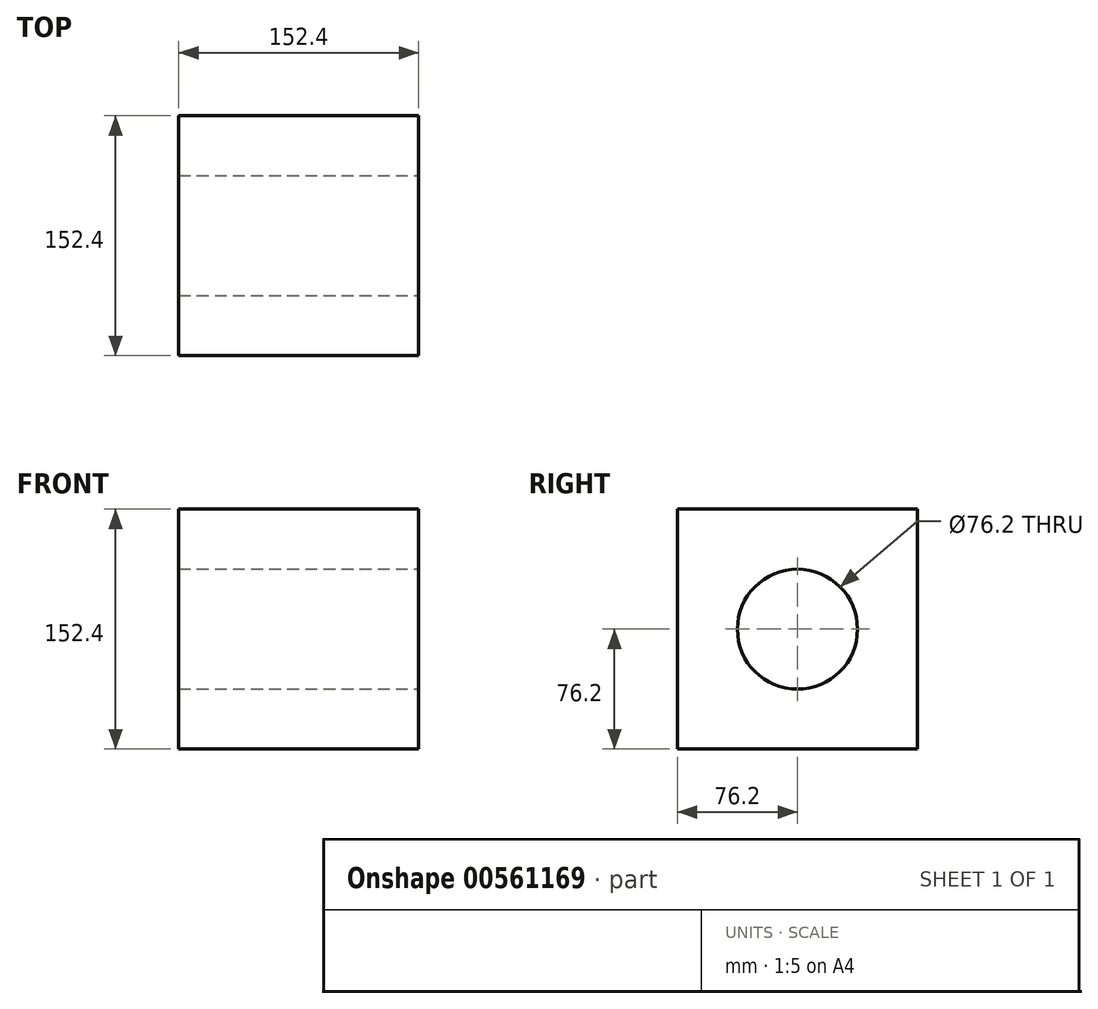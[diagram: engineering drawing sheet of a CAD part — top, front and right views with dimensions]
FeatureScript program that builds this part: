
annotation { "Feature Type Name" : "Feature", "Feature Type Description" : "" }
export const myFeature = defineFeature(function(context is Context, id is Id, definition is map)
    precondition{}
    {
        {
            var Q0;
            Q0=qCreatedBy(makeId("Top.planeOp"),FACE);
            var sketch = newSketch(context, id + "F0", { "sketchPlane" : qUnion([Q0])});
            skLineSegment(sketch, "E0.bottom", {"start": v(76.2, 76.2) * mm, "end": v(-76.2, 76.2) * mm});
            skLineSegment(sketch, "E0.top", {"start": v(76.2, -76.2) * mm, "end": v(-76.2, -76.2) * mm});
            skLineSegment(sketch, "E0.left", {"start": v(76.2, 76.2) * mm, "end": v(76.2, -76.2) * mm});
            skLineSegment(sketch, "E0.right", {"start": v(-76.2, 76.2) * mm, "end": v(-76.2, -76.2) * mm});
            skPoint(sketch, "E0.middle", {"position": v(0, 0) * mm});
            skSolve(sketch);
        }
        {
            var Q0;
            Q0=makeQuery(id+"F0.imprint","IMPRINT",FACE,{"disambiguationData":[TD([[makeQuery(id+"F0.imprint","IMPRINT",EDGE,{"derivedFrom":sQuery(id+"F0.wireOp",EDGE,"E0.bottom")}),1.0]])]});
            extrude(context, id + "F1", {"entities" : qUnion([Q0]), "depth" : 152.4 * mm, "offsetDistance" : 25.4 * mm});
        }
        {
            var Q0;
            Q0=makeQuery(id+"F1.opExtrude","SWEPT_FACE",FACE,{"disambiguationData":[OSD([sQuery(id+"F0.wireOp",EDGE,"E0.left")])]});
            var sketch = newSketch(context, id + "F2", { "sketchPlane" : qUnion([Q0])});
            skCircle(sketch, "E1", {"center": v(0, 76.2) * mm, "radius": 38.1 * mm});
            skPoint(sketch, "E1.centerSnap0", {"position": v(-76.2, 76.2) * mm});
            skSolve(sketch);
        }
        {
            var Q0;
            Q0 = qSketchRegion(id + "F2", true);
            extrude(context, id + "F3", {"entities" : qUnion([Q0]), "operationType" : NewBodyOperationType.REMOVE, "endBound" : BoundingType.THROUGH_ALL, "oppositeDirection" : true, "depth" : 152.4 * mm, "offsetDistance" : 25.4 * mm});
        }
    });
